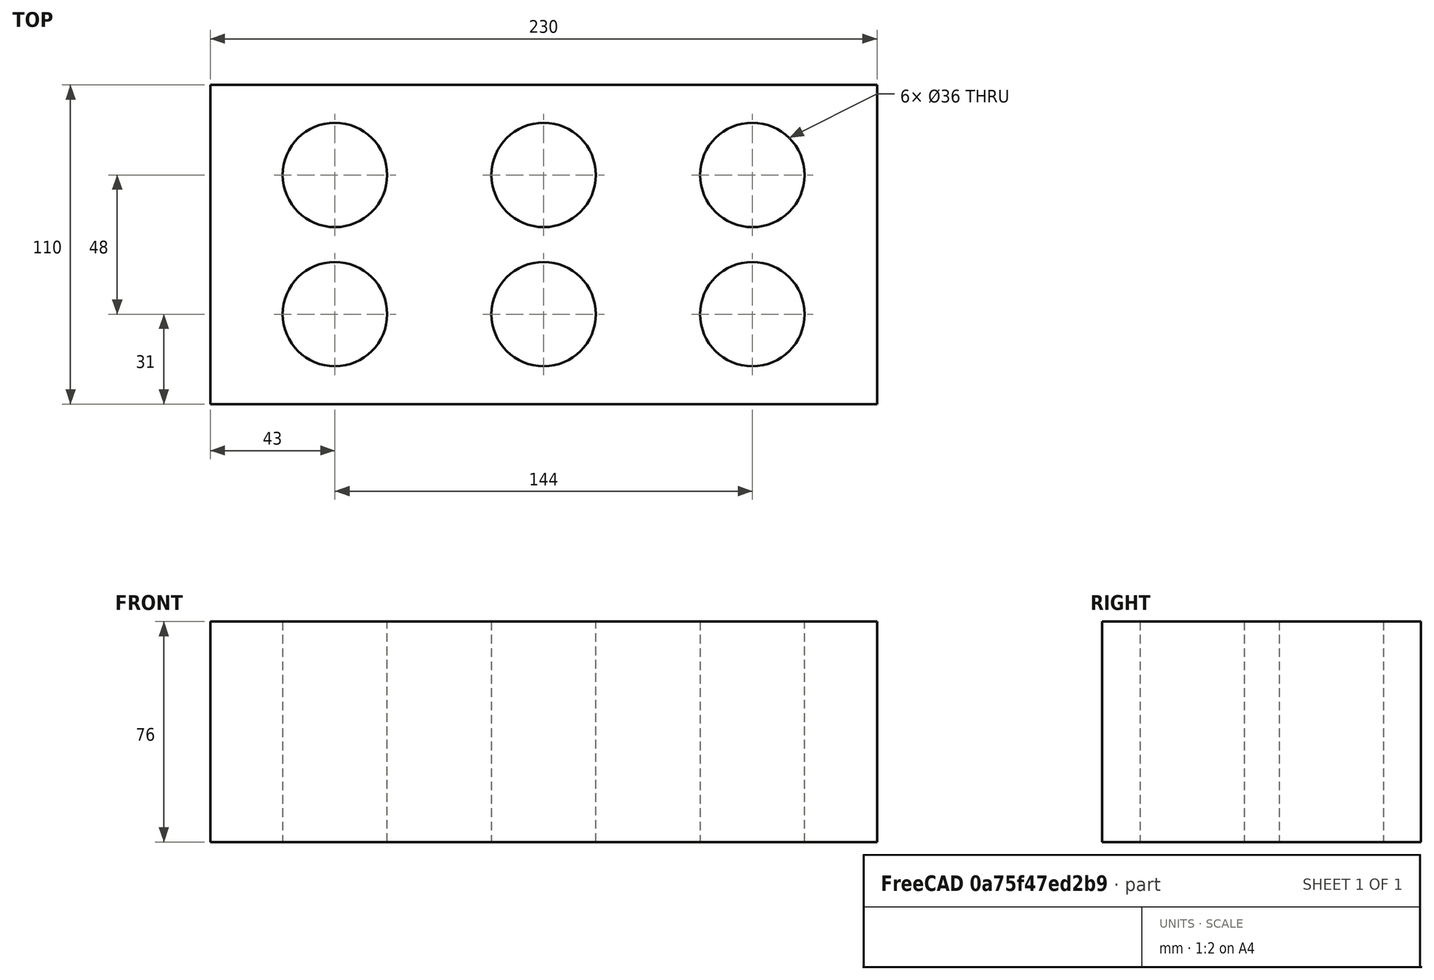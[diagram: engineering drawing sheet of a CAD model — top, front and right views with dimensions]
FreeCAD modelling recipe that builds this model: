
FCSTD DOCUMENT  (FreeCAD 1.0R39285 (Git))
Label: ojt1_t09r02_brick
License: All rights reserved
objects: Part::Cylinder×6, Part::Box×1, Part::MultiFuse×1, Part::Cut×1
note: 9 computed .brp shape members not serialized (recipe doc carries the construction recipe); baked Part::Feature solids carry a one-line shape summary decoded from their .brp

FEATURE [Part::Cylinder] Cylinder  label="Cilindre"
  Angle = 360
  AttacherType = Attacher::AttachEngine3D
  FirstAngle = 0
  Height = 80
  Placement = pos=(43,31,-2) rot=(0,0,1;0rad)
  Radius = 18
  SecondAngle = 0
FEATURE [Part::Cylinder] Cylinder001  label="Cilindre001"
  Angle = 360
  AttacherType = Attacher::AttachEngine3D
  FirstAngle = 0
  Height = 80
  Placement = pos=(43,79,-2) rot=(0,0,1;0rad)
  Radius = 18
  SecondAngle = 0
FEATURE [Part::Cylinder] Cylinder002  label="Cilindre002"
  Angle = 360
  AttacherType = Attacher::AttachEngine3D
  FirstAngle = 0
  Height = 80
  Placement = pos=(187,79,-2) rot=(0,0,1;0rad)
  Radius = 18
  SecondAngle = 0
FEATURE [Part::Cylinder] Cylinder003  label="Cilindre003"
  Angle = 360
  AttacherType = Attacher::AttachEngine3D
  FirstAngle = 0
  Height = 80
  Placement = pos=(115,31,-2) rot=(0,0,1;0rad)
  Radius = 18
  SecondAngle = 0
FEATURE [Part::Cylinder] Cylinder004  label="Cilindre004"
  Angle = 360
  AttacherType = Attacher::AttachEngine3D
  FirstAngle = 0
  Height = 80
  Placement = pos=(115,79,-2) rot=(0,0,1;0rad)
  Radius = 18
  SecondAngle = 0
FEATURE [Part::Cylinder] Cylinder005  label="Cilindre005"
  Angle = 360
  AttacherType = Attacher::AttachEngine3D
  FirstAngle = 0
  Height = 80
  Placement = pos=(187,31,-2) rot=(0,0,1;0rad)
  Radius = 18
  SecondAngle = 0
FEATURE [Part::Box] Box  label="basis"
  AttacherType = Attacher::AttachEngine3D
  Height = 76
  Length = 230
  Width = 110
FEATURE [Part::MultiFuse] Fusion
  Refine = true
  Shapes = -> [Cylinder,Cylinder001,Cylinder002,Cylinder003,Cylinder004,Cylinder005]
FEATURE [Part::Cut] Cut  label="brick"
  Base = -> Box
  Refine = true
  Tool = -> Fusion
